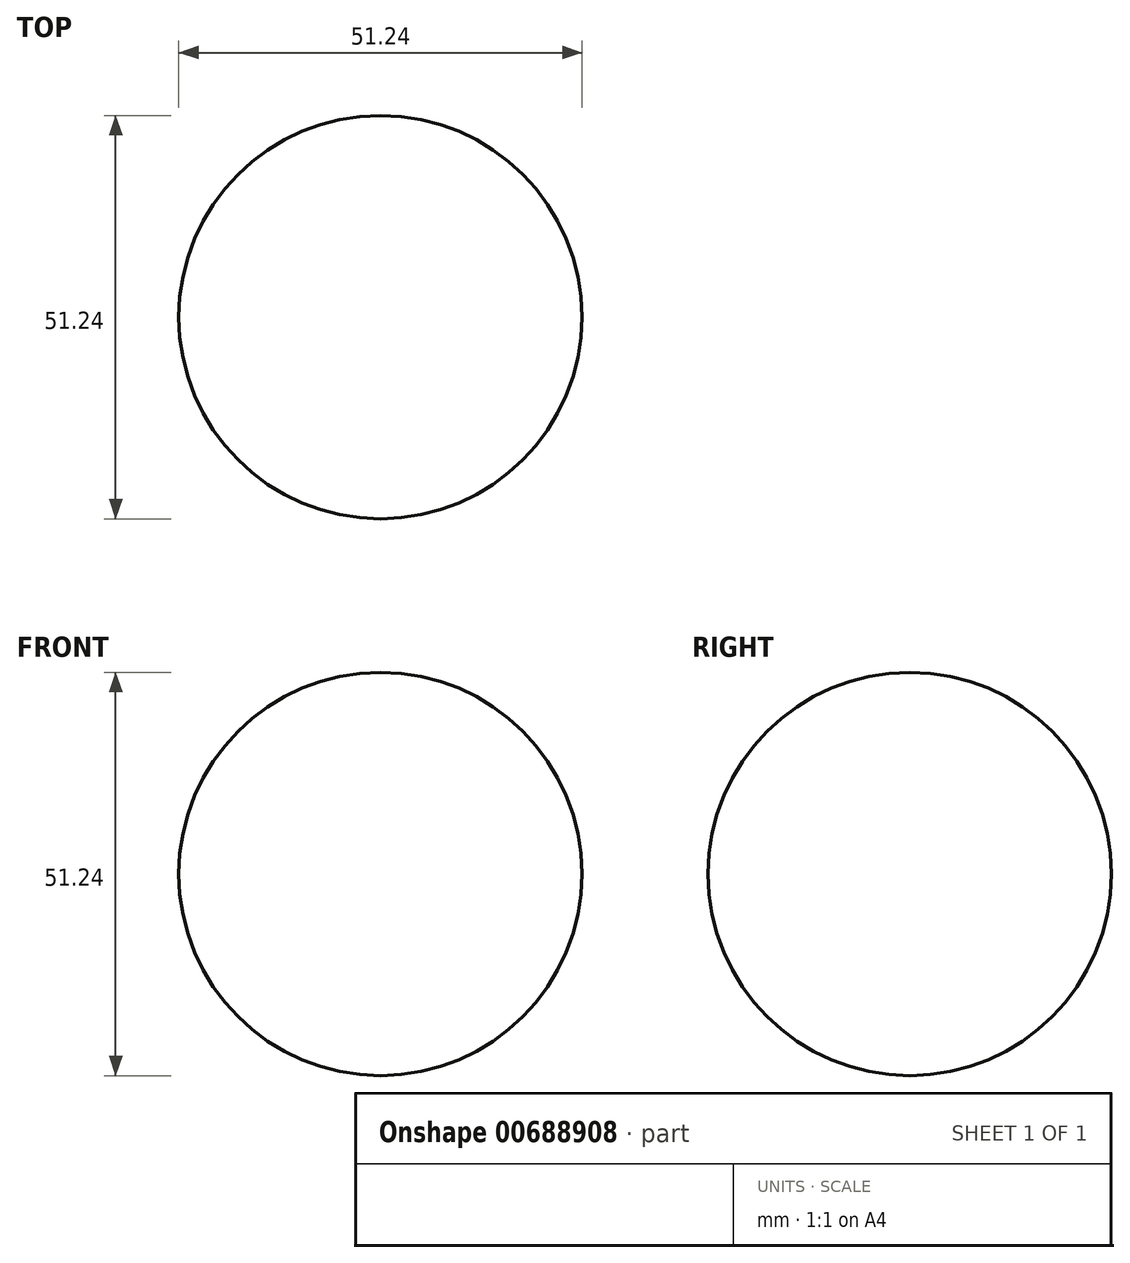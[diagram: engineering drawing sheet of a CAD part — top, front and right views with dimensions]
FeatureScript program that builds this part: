
annotation { "Feature Type Name" : "Feature", "Feature Type Description" : "" }
export const myFeature = defineFeature(function(context is Context, id is Id, definition is map)
    precondition{}
    {
        {
            var Q0;
            Q0=qCreatedBy(makeId("Top.planeOp"),FACE);
            var sketch = newSketch(context, id + "F0", { "sketchPlane" : qUnion([Q0])});
            skArc(sketch, "E0", {"start": v(0, -25.62) * mm, "mid": v(25.62, 0) * mm, "end": v(0, 25.62) * mm});
            skLineSegment(sketch, "E1", {"start": v(0, 25.62) * mm, "end": v(0, -25.62) * mm});
            skSolve(sketch);
        }
        {
            var Q0;
            Q0 = qSketchRegion(id + "F0", true);
            var Q1;
            Q1=sQuery(id+"F0.wireOp",EDGE,"E1");
            revolve(context, id + "F1", {"entities" : qUnion([Q0]), "axis" : qUnion([Q1]), "revolveType" : RevolveType.FULL});
        }
    });
